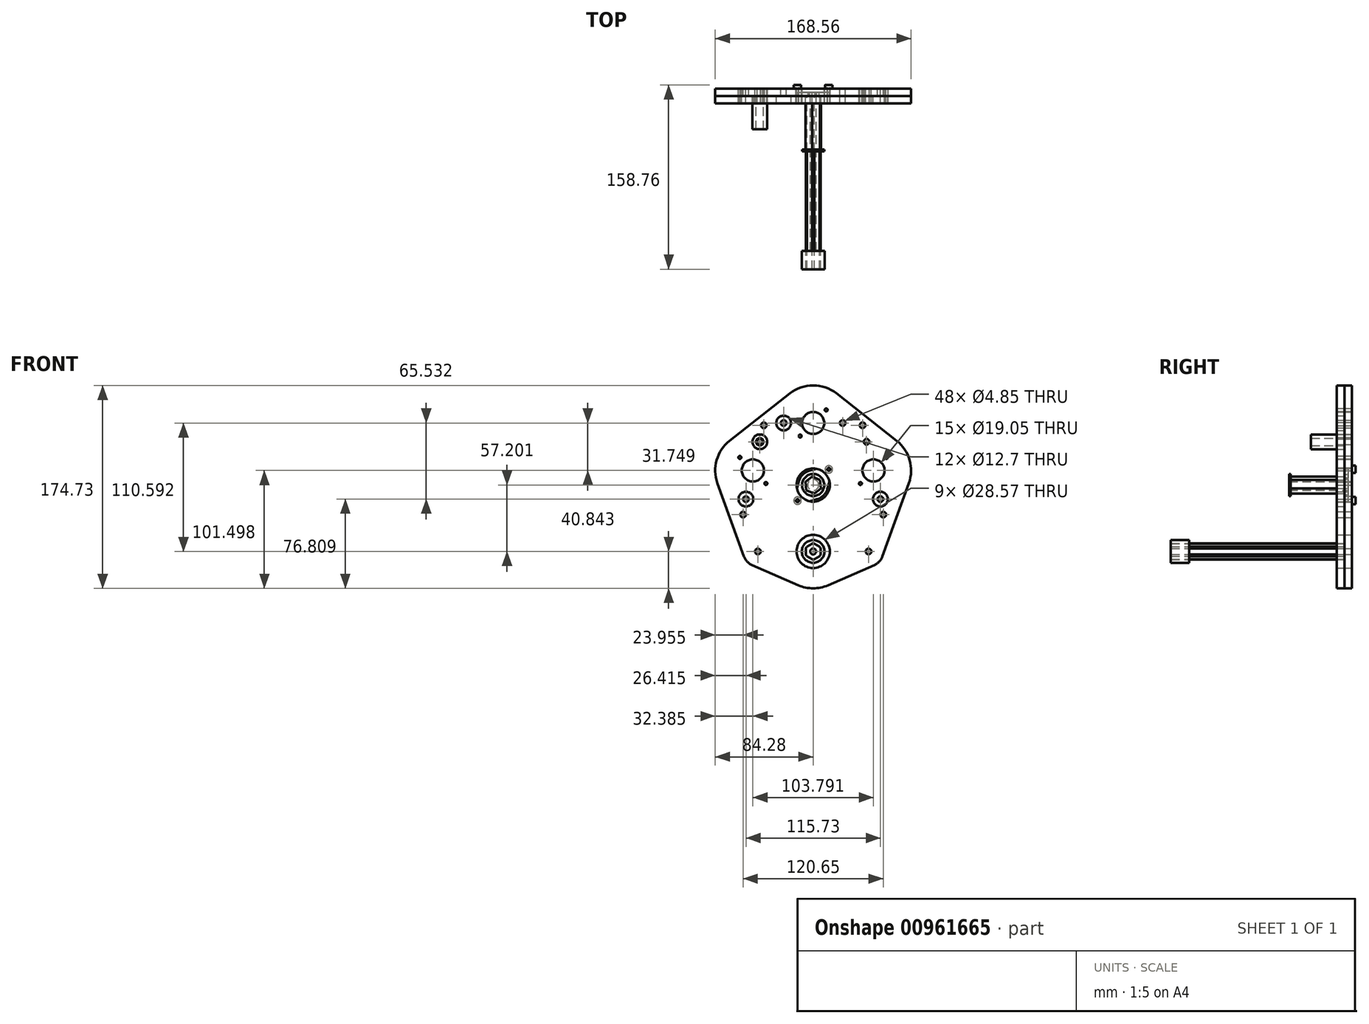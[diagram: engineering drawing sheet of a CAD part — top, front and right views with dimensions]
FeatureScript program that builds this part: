
annotation { "Feature Type Name" : "Feature", "Feature Type Description" : "" }
export const myFeature = defineFeature(function(context is Context, id is Id, definition is map)
    precondition{}
    {
        {
            var Q0;
            Q0=qCreatedBy(makeId("Front.planeOp"),FACE);
            var sketch = newSketch(context, id + "F0", { "sketchPlane" : qUnion([Q0])});
            skPoint(sketch, "E0.middle", {"position": v(0, 0) * mm});
            skCircle(sketch, "E1", {"center": v(0, 53.4) * mm, "radius": 9.53 * mm});
            skCircle(sketch, "E2", {"center": v(-51.9, 12.55) * mm, "radius": 9.53 * mm});
            skCircle(sketch, "E3", {"center": v(0, 0) * mm, "radius": 14.29 * mm});
            skCircle(sketch, "E4", {"center": v(0, -57.2) * mm, "radius": 14.29 * mm});
            skCircle(sketch, "E5", {"center": v(-25.4, 53.4) * mm, "radius": 2.43 * mm});
            skLineSegment(sketch, "E6", {"start": v(0, 0) * mm, "end": v(-51.9, 12.55) * mm, "construction": true});
            skLineSegment(sketch, "E7", {"start": v(-45.93, 37.24) * mm, "end": v(-57.86, -12.14) * mm, "construction": true});
            skCircle(sketch, "E8", {"center": v(-45.93, 37.24) * mm, "radius": 2.43 * mm});
            skCircle(sketch, "E9", {"center": v(-57.86, -12.14) * mm, "radius": 2.43 * mm});
            skCircle(sketch, "E10.MirrorC", {"center": v(45.93, 37.24) * mm, "radius": 2.43 * mm});
            skCircle(sketch, "E11.MirrorC", {"center": v(57.86, -12.14) * mm, "radius": 2.43 * mm});
            skCircle(sketch, "E12.MirrorC", {"center": v(25.4, 53.4) * mm, "radius": 2.43 * mm});
            skCircle(sketch, "E13.MirrorC", {"center": v(51.9, 12.55) * mm, "radius": 9.53 * mm});
            skCircle(sketch, "E14", {"center": v(-47.63, -57.2) * mm, "radius": 2.43 * mm});
            skCircle(sketch, "E15.MirrorC", {"center": v(47.63, -57.2) * mm, "radius": 2.43 * mm});
            skLineSegment(sketch, "E16", {"start": v(-25.4, 53.4) * mm, "end": v(25.4, 53.4) * mm, "construction": true});
            skCircle(sketch, "E17", {"center": v(0, 53.4) * mm, "radius": 32.39 * mm, "construction": true});
            skCircle(sketch, "E18", {"center": v(-51.9, 12.55) * mm, "radius": 32.39 * mm, "construction": true});
            skCircle(sketch, "E19", {"center": v(51.9, 12.55) * mm, "radius": 32.39 * mm, "construction": true});
            skLineSegment(sketch, "E20", {"start": v(-11.23, 42.17) * mm, "end": v(11.23, 64.62) * mm, "construction": true});
            skCircle(sketch, "E21", {"center": v(-11.23, 42.17) * mm, "radius": 1.27 * mm});
            skCircle(sketch, "E22", {"center": v(11.23, 64.62) * mm, "radius": 1.27 * mm});
            skPoint(sketch, "E23", {"position": v(0, 73.08) * mm});
            skLineSegment(sketch, "E24", {"start": v(-13.47, -13.47) * mm, "end": v(13.47, 13.47) * mm, "construction": true});
            skCircle(sketch, "E25", {"center": v(13.47, 13.47) * mm, "radius": 1.27 * mm});
            skCircle(sketch, "E26", {"center": v(-13.47, -13.47) * mm, "radius": 1.27 * mm});
            skLineSegment(sketch, "E27", {"start": v(-63.12, 23.77) * mm, "end": v(-40.67, 1.32) * mm, "construction": true});
            skLineSegment(sketch, "E28", {"start": v(40.67, 1.32) * mm, "end": v(63.12, 23.77) * mm, "construction": true});
            skCircle(sketch, "E29", {"center": v(-40.67, 1.32) * mm, "radius": 1.27 * mm});
            skCircle(sketch, "E30", {"center": v(-63.12, 23.77) * mm, "radius": 1.27 * mm});
            skCircle(sketch, "E31", {"center": v(63.12, 23.77) * mm, "radius": 1.27 * mm});
            skCircle(sketch, "E32", {"center": v(40.67, 1.32) * mm, "radius": 1.27 * mm});
            skCircle(sketch, "E33.0", {"center": v(0, -57.2) * mm, "radius": 31.75 * mm, "construction": true});
            skLineSegment(sketch, "E34", {"start": v(-20.03, 78.84) * mm, "end": v(-71.92, 38) * mm});
            skLineSegment(sketch, "E35", {"start": v(20.03, 78.84) * mm, "end": v(71.92, 38) * mm});
            skCircle(sketch, "E36", {"center": v(-47.63, -57.2) * mm, "radius": 12.7 * mm, "construction": true});
            skCircle(sketch, "E37", {"center": v(47.63, -57.2) * mm, "radius": 12.7 * mm, "construction": true});
            skLineSegment(sketch, "E38", {"start": v(-82.35, 1.54) * mm, "end": v(-59.57, -61.52) * mm});
            skLineSegment(sketch, "E39", {"start": v(-52.7, -68.84) * mm, "end": v(-12.7, -86.3) * mm});
            skLineSegment(sketch, "E40", {"start": v(12.7, -86.3) * mm, "end": v(52.7, -68.84) * mm});
            skLineSegment(sketch, "E41", {"start": v(59.57, -61.52) * mm, "end": v(82.35, 1.54) * mm});
            skArc(sketch, "E42", {"start": v(20.03, 78.84) * mm, "mid": v(0, 85.78) * mm, "end": v(-20.03, 78.84) * mm});
            skArc(sketch, "E43", {"start": v(82.35, 1.54) * mm, "mid": v(83.03, 21.46) * mm, "end": v(71.92, 38) * mm});
            skArc(sketch, "E44", {"start": v(52.7, -68.84) * mm, "mid": v(56.9, -65.89) * mm, "end": v(59.57, -61.52) * mm});
            skArc(sketch, "E45", {"start": v(-12.7, -86.3) * mm, "mid": v(0, -88.95) * mm, "end": v(12.7, -86.3) * mm});
            skArc(sketch, "E46", {"start": v(-59.57, -61.52) * mm, "mid": v(-56.9, -65.89) * mm, "end": v(-52.7, -68.84) * mm});
            skArc(sketch, "E47", {"start": v(-71.92, 38) * mm, "mid": v(-83.03, 21.46) * mm, "end": v(-82.35, 1.54) * mm});
            skCircle(sketch, "E48", {"center": v(-42.5, 51.43) * mm, "radius": 2.43 * mm});
            skCircle(sketch, "E49", {"center": v(-60.33, -25.45) * mm, "radius": 2.43 * mm});
            skCircle(sketch, "E50.MirrorC", {"center": v(42.5, 51.43) * mm, "radius": 2.43 * mm});
            skCircle(sketch, "E51.MirrorC", {"center": v(60.33, -25.45) * mm, "radius": 2.43 * mm});
            skLineSegment(sketch, "E52", {"start": v(-45.93, 37.24) * mm, "end": v(-42.5, 51.43) * mm, "construction": true});
            skLineSegment(sketch, "E53", {"start": v(-47.63, -57.2) * mm, "end": v(-47.63, -25.45) * mm, "construction": true});
            skLineSegment(sketch, "E54", {"start": v(-47.63, -25.45) * mm, "end": v(-60.33, -25.45) * mm, "construction": true});
            skLineSegment(sketch, "E55.bottom", {"start": v(-76.2, -31.8) * mm, "end": v(76.2, -31.8) * mm, "construction": true});
            skLineSegment(sketch, "E55.top", {"start": v(-76.2, -82.6) * mm, "end": v(76.2, -82.6) * mm, "construction": true});
            skLineSegment(sketch, "E55.left", {"start": v(-76.2, -31.8) * mm, "end": v(-76.2, -82.6) * mm, "construction": true});
            skLineSegment(sketch, "E55.right", {"start": v(76.2, -31.8) * mm, "end": v(76.2, -82.6) * mm, "construction": true});
            skPoint(sketch, "E56", {"position": v(76.2, -57.2) * mm});
            skPoint(sketch, "E57", {"position": v(0, -82.6) * mm});
            skSolve(sketch);
        }
        {
            var Q0;
            Q0=makeQuery(id+"F0.imprint","IMPRINT",FACE,{"disambiguationData":[TD([[makeQuery(id+"F0.imprint","IMPRINT",EDGE,{"derivedFrom":sQuery(id+"F0.wireOp",EDGE,"E1")}),-1.0]])]});
            extrude(context, id + "F1", {"entities" : qUnion([Q0]), "depth" : 6.35 * mm, "offsetDistance" : 25.4 * mm});
        }
        {
            var Q0;
            Q0=makeQuery(id+"F1.opExtrude","CAP_FACE",FACE,{"disambiguationData":[OSD([sQuery(id+"F0.wireOp",EDGE,"E1"),sQuery(id+"F0.wireOp",EDGE,"E2"),sQuery(id+"F0.wireOp",EDGE,"v2gbIf3F-sjIH-0Jlf-8SnF-WHDscdTQMHb3.bottom"),sQuery(id+"F0.wireOp",EDGE,"v2gbIf3F-sjIH-0Jlf-8SnF-WHDscdTQMHb3.top"),sQuery(id+"F0.wireOp",EDGE,"v2gbIf3F-sjIH-0Jlf-8SnF-WHDscdTQMHb3.left"),sQuery(id+"F0.wireOp",EDGE,"v2gbIf3F-sjIH-0Jlf-8SnF-WHDscdTQMHb3.right"),sQuery(id+"F0.wireOp",EDGE,"E3"),sQuery(id+"F0.wireOp",EDGE,"E4"),sQuery(id+"F0.wireOp",EDGE,"E5"),sQuery(id+"F0.wireOp",EDGE,"E8"),sQuery(id+"F0.wireOp",EDGE,"E9"),sQuery(id+"F0.wireOp",EDGE,"E10.MirrorC"),sQuery(id+"F0.wireOp",EDGE,"E11.MirrorC"),sQuery(id+"F0.wireOp",EDGE,"E12.MirrorC"),sQuery(id+"F0.wireOp",EDGE,"9f56034d-28e1-4162-898a-95c3412c0e040.MirrorCS"),sQuery(id+"F0.wireOp",EDGE,"273e83dc-7785-426b-80ec-8bf11da8723f0.MirrorCS"),sQuery(id+"F0.wireOp",EDGE,"E13.MirrorC")])],"isStart":false});
            var sketch = newSketch(context, id + "F2", { "sketchPlane" : qUnion([Q0])});
            skCircle(sketch, "E58", {"center": v(-45.93, 37.24) * mm, "radius": 6.35 * mm});
            skCircle(sketch, "E59", {"center": v(-45.93, 37.24) * mm, "radius": 3.18 * mm});
            skSolve(sketch);
        }
        {
            var Q0;
            Q0=qSketchRegion(id+"F2",true);
            extrude(context, id + "F3", {"entities" : qUnion([Q0]), "depth" : 28.75 * mm, "offsetDistance" : 25.4 * mm});
        }
        {
            var Q0;
            Q0=makeQuery(id+"F1.opExtrude","CAP_FACE",FACE,{"disambiguationData":[OSD([sQuery(id+"F0.wireOp",EDGE,"E1"),sQuery(id+"F0.wireOp",EDGE,"E2"),sQuery(id+"F0.wireOp",EDGE,"E3"),sQuery(id+"F0.wireOp",EDGE,"E4"),sQuery(id+"F0.wireOp",EDGE,"E5"),sQuery(id+"F0.wireOp",EDGE,"E8"),sQuery(id+"F0.wireOp",EDGE,"E9"),sQuery(id+"F0.wireOp",EDGE,"E10.MirrorC"),sQuery(id+"F0.wireOp",EDGE,"E11.MirrorC"),sQuery(id+"F0.wireOp",EDGE,"E12.MirrorC"),sQuery(id+"F0.wireOp",EDGE,"E13.MirrorC"),sQuery(id+"F0.wireOp",EDGE,"E14"),sQuery(id+"F0.wireOp",EDGE,"E15.MirrorC"),sQuery(id+"F0.wireOp",EDGE,"Ia5A7rCy-c0Ep-uM7U-ytcM-FB4trdygkSBH.bottom"),sQuery(id+"F0.wireOp",EDGE,"Ia5A7rCy-c0Ep-uM7U-ytcM-FB4trdygkSBH.top"),sQuery(id+"F0.wireOp",EDGE,"Ia5A7rCy-c0Ep-uM7U-ytcM-FB4trdygkSBH.left"),sQuery(id+"F0.wireOp",EDGE,"Ia5A7rCy-c0Ep-uM7U-ytcM-FB4trdygkSBH.right"),sQuery(id+"F0.wireOp",EDGE,"9hy43MYI-83Wv-VwrP-aWnk-op4wOjKTtN4z"),sQuery(id+"F0.wireOp",EDGE,"cf7caecd-f94a-49e7-b14e-7d0b33bf44ac0.MirrorC"),sQuery(id+"F0.wireOp",EDGE,"VPC0NVVz-Sinw-XyrT-1Bkp-COakgAjF56Cj"),sQuery(id+"F0.wireOp",EDGE,"f5847759-d2b6-4925-87d4-92d8143ec5020.MirrorC"),sQuery(id+"F0.wireOp",EDGE,"E21"),sQuery(id+"F0.wireOp",EDGE,"E22"),sQuery(id+"F0.wireOp",EDGE,"3fPKynrt-P6VC-zHZV-j1N4-QmUOg58pSjru"),sQuery(id+"F0.wireOp",EDGE,"B02TouvB-5slD-eYO9-rdQn-fII5tJYorJ8w")])],"isStart":false});
            var sketch = newSketch(context, id + "F4", { "sketchPlane" : qUnion([Q0])});
            skCircle(sketch, "E60.cCircle", {"center": v(0, 0) * mm, "radius": 6.35 * mm, "construction": true});
            skLineSegment(sketch, "E60.0", {"start": v(6.75, -2.87) * mm, "end": v(0.89, -7.28) * mm});
            skLineSegment(sketch, "E60.1", {"start": v(0.89, -7.28) * mm, "end": v(-5.86, -4.4) * mm});
            skLineSegment(sketch, "E60.2", {"start": v(-5.86, -4.4) * mm, "end": v(-6.75, 2.87) * mm});
            skLineSegment(sketch, "E60.3", {"start": v(-6.75, 2.87) * mm, "end": v(-0.89, 7.28) * mm});
            skLineSegment(sketch, "E60.4", {"start": v(-0.89, 7.28) * mm, "end": v(5.86, 4.4) * mm});
            skLineSegment(sketch, "E60.5", {"start": v(5.86, 4.4) * mm, "end": v(6.75, -2.87) * mm});
            skPoint(sketch, "E60.0.midPoint", {"position": v(3.82, -5.07) * mm});
            skSolve(sketch);
        }
        {
            var Q0;
            Q0=qSketchRegion(id+"F4",true);
            extrude(context, id + "F5", {"entities" : qUnion([Q0]), "depth" : 47.62 * mm, "offsetDistance" : 25.4 * mm});
        }
        {
            var Q0;
            Q0=makeQuery(id+"F1.opExtrude","CAP_FACE",FACE,{"disambiguationData":[OSD([sQuery(id+"F0.wireOp",EDGE,"E1"),sQuery(id+"F0.wireOp",EDGE,"E2"),sQuery(id+"F0.wireOp",EDGE,"E3"),sQuery(id+"F0.wireOp",EDGE,"E4"),sQuery(id+"F0.wireOp",EDGE,"E5"),sQuery(id+"F0.wireOp",EDGE,"E8"),sQuery(id+"F0.wireOp",EDGE,"E9"),sQuery(id+"F0.wireOp",EDGE,"E10.MirrorC"),sQuery(id+"F0.wireOp",EDGE,"E11.MirrorC"),sQuery(id+"F0.wireOp",EDGE,"E12.MirrorC"),sQuery(id+"F0.wireOp",EDGE,"E13.MirrorC"),sQuery(id+"F0.wireOp",EDGE,"E14"),sQuery(id+"F0.wireOp",EDGE,"E15.MirrorC"),sQuery(id+"F0.wireOp",EDGE,"Ia5A7rCy-c0Ep-uM7U-ytcM-FB4trdygkSBH.bottom"),sQuery(id+"F0.wireOp",EDGE,"Ia5A7rCy-c0Ep-uM7U-ytcM-FB4trdygkSBH.top"),sQuery(id+"F0.wireOp",EDGE,"Ia5A7rCy-c0Ep-uM7U-ytcM-FB4trdygkSBH.left"),sQuery(id+"F0.wireOp",EDGE,"Ia5A7rCy-c0Ep-uM7U-ytcM-FB4trdygkSBH.right"),sQuery(id+"F0.wireOp",EDGE,"9hy43MYI-83Wv-VwrP-aWnk-op4wOjKTtN4z"),sQuery(id+"F0.wireOp",EDGE,"cf7caecd-f94a-49e7-b14e-7d0b33bf44ac0.MirrorC"),sQuery(id+"F0.wireOp",EDGE,"VPC0NVVz-Sinw-XyrT-1Bkp-COakgAjF56Cj"),sQuery(id+"F0.wireOp",EDGE,"f5847759-d2b6-4925-87d4-92d8143ec5020.MirrorC"),sQuery(id+"F0.wireOp",EDGE,"E21"),sQuery(id+"F0.wireOp",EDGE,"E22"),sQuery(id+"F0.wireOp",EDGE,"3fPKynrt-P6VC-zHZV-j1N4-QmUOg58pSjru"),sQuery(id+"F0.wireOp",EDGE,"B02TouvB-5slD-eYO9-rdQn-fII5tJYorJ8w")])],"isStart":false});
            var sketch = newSketch(context, id + "F6", { "sketchPlane" : qUnion([Q0])});
            skCircle(sketch, "E61.cCircle", {"center": v(0, -57.2) * mm, "radius": 6.35 * mm, "construction": true});
            skLineSegment(sketch, "E61.0", {"start": v(6.35, -60.87) * mm, "end": v(0, -64.53) * mm});
            skLineSegment(sketch, "E61.1", {"start": v(0, -64.53) * mm, "end": v(-6.35, -60.87) * mm});
            skLineSegment(sketch, "E61.2", {"start": v(-6.35, -60.87) * mm, "end": v(-6.35, -53.53) * mm});
            skLineSegment(sketch, "E61.3", {"start": v(-6.35, -53.53) * mm, "end": v(0, -49.87) * mm});
            skLineSegment(sketch, "E61.4", {"start": v(0, -49.87) * mm, "end": v(6.35, -53.53) * mm});
            skLineSegment(sketch, "E61.5", {"start": v(6.35, -53.53) * mm, "end": v(6.35, -60.87) * mm});
            skPoint(sketch, "E61.0.midPoint", {"position": v(3.18, -62.7) * mm});
            skCircle(sketch, "E62", {"center": v(0, -57.2) * mm, "radius": 6.88 * mm});
            skCircle(sketch, "E63", {"center": v(0, -57.2) * mm, "radius": 2.55 * mm});
            skSolve(sketch);
        }
        {
            var Q0;
            {var subQ0=sQuery(id+"F6.wireOp",EDGE,"E62");var subQ14=sQuery(id+"F6.wireOp",EDGE,"E61.0");var subQ15=makeQuery(id+"F6.imprint","INTERSECT",VERTEX,{"disambiguationData":[OD(0.0)],"derivedFrom":[subQ14,subQ0]});Q0=makeQuery(id+"F6.imprint","IMPRINT",FACE,{"disambiguationData":[TD([[makeQuery(id+"F6.imprint","IMPRINT",EDGE,{"disambiguationData":[TD([[subQ15,-1.0]])],"derivedFrom":subQ14}),-1.0]])]});}
            extrude(context, id + "F7", {"entities" : qUnion([Q0]), "depth" : 133.35 * mm, "offsetDistance" : 25.4 * mm});
        }
        {
            var Q0;
            Q0=makeQuery(id+"F1.opExtrude","CAP_FACE",FACE,{"disambiguationData":[OSD([sQuery(id+"F0.wireOp",EDGE,"E1"),sQuery(id+"F0.wireOp",EDGE,"E2"),sQuery(id+"F0.wireOp",EDGE,"E3"),sQuery(id+"F0.wireOp",EDGE,"E4"),sQuery(id+"F0.wireOp",EDGE,"E5"),sQuery(id+"F0.wireOp",EDGE,"E8"),sQuery(id+"F0.wireOp",EDGE,"E9"),sQuery(id+"F0.wireOp",EDGE,"E10.MirrorC"),sQuery(id+"F0.wireOp",EDGE,"E11.MirrorC"),sQuery(id+"F0.wireOp",EDGE,"E12.MirrorC"),sQuery(id+"F0.wireOp",EDGE,"E13.MirrorC"),sQuery(id+"F0.wireOp",EDGE,"E14"),sQuery(id+"F0.wireOp",EDGE,"E15.MirrorC"),sQuery(id+"F0.wireOp",EDGE,"Ia5A7rCy-c0Ep-uM7U-ytcM-FB4trdygkSBH.bottom"),sQuery(id+"F0.wireOp",EDGE,"Ia5A7rCy-c0Ep-uM7U-ytcM-FB4trdygkSBH.left"),sQuery(id+"F0.wireOp",EDGE,"Ia5A7rCy-c0Ep-uM7U-ytcM-FB4trdygkSBH.right"),sQuery(id+"F0.wireOp",EDGE,"9hy43MYI-83Wv-VwrP-aWnk-op4wOjKTtN4z"),sQuery(id+"F0.wireOp",EDGE,"cf7caecd-f94a-49e7-b14e-7d0b33bf44ac0.MirrorC"),sQuery(id+"F0.wireOp",EDGE,"VPC0NVVz-Sinw-XyrT-1Bkp-COakgAjF56Cj"),sQuery(id+"F0.wireOp",EDGE,"f5847759-d2b6-4925-87d4-92d8143ec5020.MirrorC"),sQuery(id+"F0.wireOp",EDGE,"E21"),sQuery(id+"F0.wireOp",EDGE,"E22"),sQuery(id+"F0.wireOp",EDGE,"3fPKynrt-P6VC-zHZV-j1N4-QmUOg58pSjru"),sQuery(id+"F0.wireOp",EDGE,"B02TouvB-5slD-eYO9-rdQn-fII5tJYorJ8w"),sQuery(id+"F0.wireOp",EDGE,"E25"),sQuery(id+"F0.wireOp",EDGE,"E26"),sQuery(id+"F0.wireOp",EDGE,"E29"),sQuery(id+"F0.wireOp",EDGE,"E30"),sQuery(id+"F0.wireOp",EDGE,"E31"),sQuery(id+"F0.wireOp",EDGE,"E32"),sQuery(id+"F0.wireOp",EDGE,"aEMf5mhu-Wrcx-876B-wnVO-35Rc34H002yA"),sQuery(id+"F0.wireOp",EDGE,"46e10e25-2245-48dc-8db0-358fd27fbfdb.1.0"),sQuery(id+"F0.wireOp",EDGE,"46e10e25-2245-48dc-8db0-358fd27fbfdb.2.0"),sQuery(id+"F0.wireOp",EDGE,"46e10e25-2245-48dc-8db0-358fd27fbfdb.3.0"),sQuery(id+"F0.wireOp",EDGE,"46e10e25-2245-48dc-8db0-358fd27fbfdb.4.0"),sQuery(id+"F0.wireOp",EDGE,"46e10e25-2245-48dc-8db0-358fd27fbfdb.5.0"),sQuery(id+"F0.wireOp",EDGE,"L9scNa7y-PHnz-kpIB-lI0T-bNJJRzmYsqX9"),sQuery(id+"F0.wireOp",EDGE,"qHdCpmer-wj71-Vpwn-qQ25-4L3qCu6oYEpw"),sQuery(id+"F0.wireOp",EDGE,"qUifEb6M-PTzv-bZuZ-YapP-IAsJ3ShUQvB8")])],"isStart":false});
            var sketch = newSketch(context, id + "F8", { "sketchPlane" : qUnion([Q0])});
            skCircle(sketch, "E64", {"center": v(-57.86, -12.14) * mm, "radius": 6.35 * mm});
            skCircle(sketch, "E65", {"center": v(57.86, -12.14) * mm, "radius": 6.35 * mm});
            skCircle(sketch, "E66", {"center": v(-25.4, 53.4) * mm, "radius": 6.35 * mm});
            skSolve(sketch);
        }
        {
            var Q0;
            Q0=makeQuery(id+"F8.imprint","IMPRINT",FACE,{"disambiguationData":[TD([[makeQuery(id+"F8.imprint","IMPRINT",EDGE,{"derivedFrom":sQuery(id+"F8.wireOp",EDGE,"E64")}),-1.0]])]});
            extrude(context, id + "F9", {"entities" : qUnion([Q0]), "depth" : 6.35 * mm, "offsetDistance" : 25.4 * mm});
        }
        {
            var Q0;
            Q0=makeQuery(id+"F7.opExtrude","CAP_FACE",FACE,{"disambiguationData":[OSD([sQuery(id+"F6.wireOp",EDGE,"E61.0"),sQuery(id+"F6.wireOp",EDGE,"E61.1"),sQuery(id+"F6.wireOp",EDGE,"E61.2"),sQuery(id+"F6.wireOp",EDGE,"E61.3"),sQuery(id+"F6.wireOp",EDGE,"E61.4"),sQuery(id+"F6.wireOp",EDGE,"E61.5"),sQuery(id+"F6.wireOp",EDGE,"E62")])],"isStart":false});
            var sketch = newSketch(context, id + "F10", { "sketchPlane" : qUnion([Q0])});
            skCircle(sketch, "E67", {"center": v(0, -57.2) * mm, "radius": 9.75 * mm});
            skSolve(sketch);
        }
        {
            var Q0;
            Q0=makeQuery(id+"F10.imprint","IMPRINT",FACE,{"disambiguationData":[TD([[makeQuery(id+"F10.imprint","IMPRINT",EDGE,{"derivedFrom":sQuery(id+"F10.wireOp",EDGE,"E67")}),1.0]])]});
            extrude(context, id + "F11", {"entities" : qUnion([Q0]), "depth" : 15.88 * mm, "offsetDistance" : 25.4 * mm});
        }
        {
            var Q0;
            Q0=makeQuery(id+"F5.opExtrude","CAP_FACE",FACE,{"disambiguationData":[OSD([sQuery(id+"F4.wireOp",EDGE,"E60.0"),sQuery(id+"F4.wireOp",EDGE,"E60.1"),sQuery(id+"F4.wireOp",EDGE,"E60.2"),sQuery(id+"F4.wireOp",EDGE,"E60.3"),sQuery(id+"F4.wireOp",EDGE,"E60.4"),sQuery(id+"F4.wireOp",EDGE,"E60.5")])],"isStart":false});
            var sketch = newSketch(context, id + "F12", { "sketchPlane" : qUnion([Q0])});
            skCircle(sketch, "E68", {"center": v(0, 0) * mm, "radius": 9.53 * mm});
            skCircle(sketch, "E69.cCircle", {"center": v(0, 0) * mm, "radius": 6.35 * mm, "construction": true});
            skLineSegment(sketch, "E69.0", {"start": v(6.75, -2.87) * mm, "end": v(0.89, -7.28) * mm});
            skLineSegment(sketch, "E69.1", {"start": v(0.89, -7.28) * mm, "end": v(-5.86, -4.4) * mm});
            skLineSegment(sketch, "E69.2", {"start": v(-5.86, -4.4) * mm, "end": v(-6.75, 2.87) * mm});
            skLineSegment(sketch, "E69.3", {"start": v(-6.75, 2.87) * mm, "end": v(-0.89, 7.28) * mm});
            skLineSegment(sketch, "E69.4", {"start": v(-0.89, 7.28) * mm, "end": v(5.86, 4.4) * mm});
            skLineSegment(sketch, "E69.5", {"start": v(5.86, 4.4) * mm, "end": v(6.75, -2.87) * mm});
            skPoint(sketch, "E69.0.midPoint", {"position": v(3.82, -5.07) * mm});
            skSolve(sketch);
        }
        {
            var Q0;
            Q0=qSketchRegion(id+"F12",true);
            extrude(context, id + "F13", {"entities" : qUnion([Q0]), "oppositeDirection" : true, "depth" : 1.59 * mm, "offsetDistance" : 25.4 * mm});
        }
        {
            var Q0;
            Q0=makeQuery(id+"F9.opExtrude","CAP_FACE",FACE,{"disambiguationData":[OSD([sQuery(id+"F0.wireOp",EDGE,"E1"),sQuery(id+"F0.wireOp",EDGE,"E2"),sQuery(id+"F0.wireOp",EDGE,"E3"),sQuery(id+"F0.wireOp",EDGE,"E4"),sQuery(id+"F0.wireOp",EDGE,"E5"),sQuery(id+"F0.wireOp",EDGE,"E8"),sQuery(id+"F0.wireOp",EDGE,"E9"),sQuery(id+"F0.wireOp",EDGE,"E10.MirrorC"),sQuery(id+"F0.wireOp",EDGE,"E11.MirrorC"),sQuery(id+"F0.wireOp",EDGE,"E12.MirrorC"),sQuery(id+"F0.wireOp",EDGE,"E13.MirrorC"),sQuery(id+"F0.wireOp",EDGE,"E14"),sQuery(id+"F0.wireOp",EDGE,"E15.MirrorC"),sQuery(id+"F0.wireOp",EDGE,"Ia5A7rCy-c0Ep-uM7U-ytcM-FB4trdygkSBH.bottom"),sQuery(id+"F0.wireOp",EDGE,"Ia5A7rCy-c0Ep-uM7U-ytcM-FB4trdygkSBH.left"),sQuery(id+"F0.wireOp",EDGE,"Ia5A7rCy-c0Ep-uM7U-ytcM-FB4trdygkSBH.right"),sQuery(id+"F0.wireOp",EDGE,"9hy43MYI-83Wv-VwrP-aWnk-op4wOjKTtN4z"),sQuery(id+"F0.wireOp",EDGE,"cf7caecd-f94a-49e7-b14e-7d0b33bf44ac0.MirrorC"),sQuery(id+"F0.wireOp",EDGE,"VPC0NVVz-Sinw-XyrT-1Bkp-COakgAjF56Cj"),sQuery(id+"F0.wireOp",EDGE,"f5847759-d2b6-4925-87d4-92d8143ec5020.MirrorC"),sQuery(id+"F0.wireOp",EDGE,"E21"),sQuery(id+"F0.wireOp",EDGE,"E22"),sQuery(id+"F0.wireOp",EDGE,"3fPKynrt-P6VC-zHZV-j1N4-QmUOg58pSjru"),sQuery(id+"F0.wireOp",EDGE,"B02TouvB-5slD-eYO9-rdQn-fII5tJYorJ8w"),sQuery(id+"F0.wireOp",EDGE,"E25"),sQuery(id+"F0.wireOp",EDGE,"E26"),sQuery(id+"F0.wireOp",EDGE,"E29"),sQuery(id+"F0.wireOp",EDGE,"E30"),sQuery(id+"F0.wireOp",EDGE,"E31"),sQuery(id+"F0.wireOp",EDGE,"E32"),sQuery(id+"F0.wireOp",EDGE,"46e10e25-2245-48dc-8db0-358fd27fbfdb.1.0"),sQuery(id+"F0.wireOp",EDGE,"46e10e25-2245-48dc-8db0-358fd27fbfdb.2.0"),sQuery(id+"F0.wireOp",EDGE,"46e10e25-2245-48dc-8db0-358fd27fbfdb.4.0"),sQuery(id+"F0.wireOp",EDGE,"46e10e25-2245-48dc-8db0-358fd27fbfdb.5.0"),sQuery(id+"F0.wireOp",EDGE,"L9scNa7y-PHnz-kpIB-lI0T-bNJJRzmYsqX9"),sQuery(id+"F0.wireOp",EDGE,"qHdCpmer-wj71-Vpwn-qQ25-4L3qCu6oYEpw"),sQuery(id+"F0.wireOp",EDGE,"qUifEb6M-PTzv-bZuZ-YapP-IAsJ3ShUQvB8"),sQuery(id+"F0.wireOp",EDGE,"L05DpjwD-QDcr-wEKk-ETSS-m0RbfmUCJncL"),sQuery(id+"F0.wireOp",EDGE,"zRujsg1A-CT0h-14dK-YTpM-AVabi17qy5bU"),sQuery(id+"F8.wireOp",EDGE,"E64"),sQuery(id+"F8.wireOp",EDGE,"E65"),sQuery(id+"F8.wireOp",EDGE,"E66")])],"isStart":true});
            var sketch = newSketch(context, id + "F14", { "sketchPlane" : qUnion([Q0])});
            skCircle(sketch, "E70", {"center": v(-13.47, 13.47) * mm, "radius": 3.18 * mm, "construction": true});
            skCircle(sketch, "E71", {"center": v(13.47, -13.47) * mm, "radius": 3.18 * mm, "construction": true});
            skCircle(sketch, "E72", {"center": v(0, 0) * mm, "radius": 12.7 * mm, "construction": true});
            skLineSegment(sketch, "E73", {"start": v(-16.54, 12.65) * mm, "end": v(-12.27, -3.29) * mm});
            skLineSegment(sketch, "E74", {"start": v(-3.29, -12.27) * mm, "end": v(12.65, -16.54) * mm});
            skLineSegment(sketch, "E75", {"start": v(16.54, -12.65) * mm, "end": v(12.27, 3.29) * mm});
            skLineSegment(sketch, "E76", {"start": v(-12.65, 16.54) * mm, "end": v(3.29, 12.27) * mm});
            skArc(sketch, "E77", {"start": v(-12.65, 16.54) * mm, "mid": v(-15.72, 15.72) * mm, "end": v(-16.54, 12.65) * mm});
            skArc(sketch, "E78", {"start": v(12.65, -16.54) * mm, "mid": v(15.72, -15.72) * mm, "end": v(16.54, -12.65) * mm});
            skArc(sketch, "E79", {"start": v(12.27, 3.29) * mm, "mid": v(8.98, 8.98) * mm, "end": v(3.29, 12.27) * mm});
            skArc(sketch, "E80", {"start": v(-12.27, -3.29) * mm, "mid": v(-8.98, -8.98) * mm, "end": v(-3.29, -12.27) * mm});
            skCircle(sketch, "E81", {"center": v(-13.47, 13.47) * mm, "radius": 1.27 * mm});
            skCircle(sketch, "E82", {"center": v(13.47, -13.47) * mm, "radius": 1.27 * mm});
            skCircle(sketch, "E83", {"center": v(0, 7.44) * mm, "radius": 1.32 * mm});
            skCircle(sketch, "E84", {"center": v(0, -7.44) * mm, "radius": 1.32 * mm});
            skLineSegment(sketch, "E85", {"start": v(0, 7.44) * mm, "end": v(0, -7.44) * mm, "construction": true});
            skCircle(sketch, "E86", {"center": v(0, 0) * mm, "radius": 4.76 * mm});
            skSolve(sketch);
        }
        {
            var Q0;
            Q0=qSketchRegion(id+"F14",true);
            extrude(context, id + "F15", {"entities" : qUnion([Q0]), "depth" : 3.17 * mm, "offsetDistance" : 25.4 * mm});
        }
        {
            var Q0;
            Q0=makeQuery(id+"F15.opExtrude","CAP_FACE",FACE,{"disambiguationData":[OSD([sQuery(id+"F14.wireOp",EDGE,"E73"),sQuery(id+"F14.wireOp",EDGE,"E74"),sQuery(id+"F14.wireOp",EDGE,"E75"),sQuery(id+"F14.wireOp",EDGE,"E76"),sQuery(id+"F14.wireOp",EDGE,"E77"),sQuery(id+"F14.wireOp",EDGE,"E78"),sQuery(id+"F14.wireOp",EDGE,"E79"),sQuery(id+"F14.wireOp",EDGE,"E80"),sQuery(id+"F14.wireOp",EDGE,"E81"),sQuery(id+"F14.wireOp",EDGE,"E82"),sQuery(id+"F14.wireOp",EDGE,"E83"),sQuery(id+"F14.wireOp",EDGE,"E84")])],"isStart":false});
            var sketch = newSketch(context, id + "F16", { "sketchPlane" : qUnion([Q0])});
            skCircle(sketch, "E87", {"center": v(-13.47, 13.47) * mm, "radius": 3.18 * mm});
            skCircle(sketch, "E88", {"center": v(13.47, -13.47) * mm, "radius": 3.18 * mm});
            skCircle(sketch, "E89", {"center": v(-13.47, 13.47) * mm, "radius": 1.27 * mm});
            skCircle(sketch, "E90", {"center": v(13.47, -13.47) * mm, "radius": 1.27 * mm});
            skSolve(sketch);
        }
        {
            var Q0;
            Q0=qSketchRegion(id+"F16",true);
            extrude(context, id + "F17", {"entities" : qUnion([Q0]), "operationType" : NewBodyOperationType.ADD, "depth" : 6.35 * mm, "offsetDistance" : 25.4 * mm});
        }
    });
